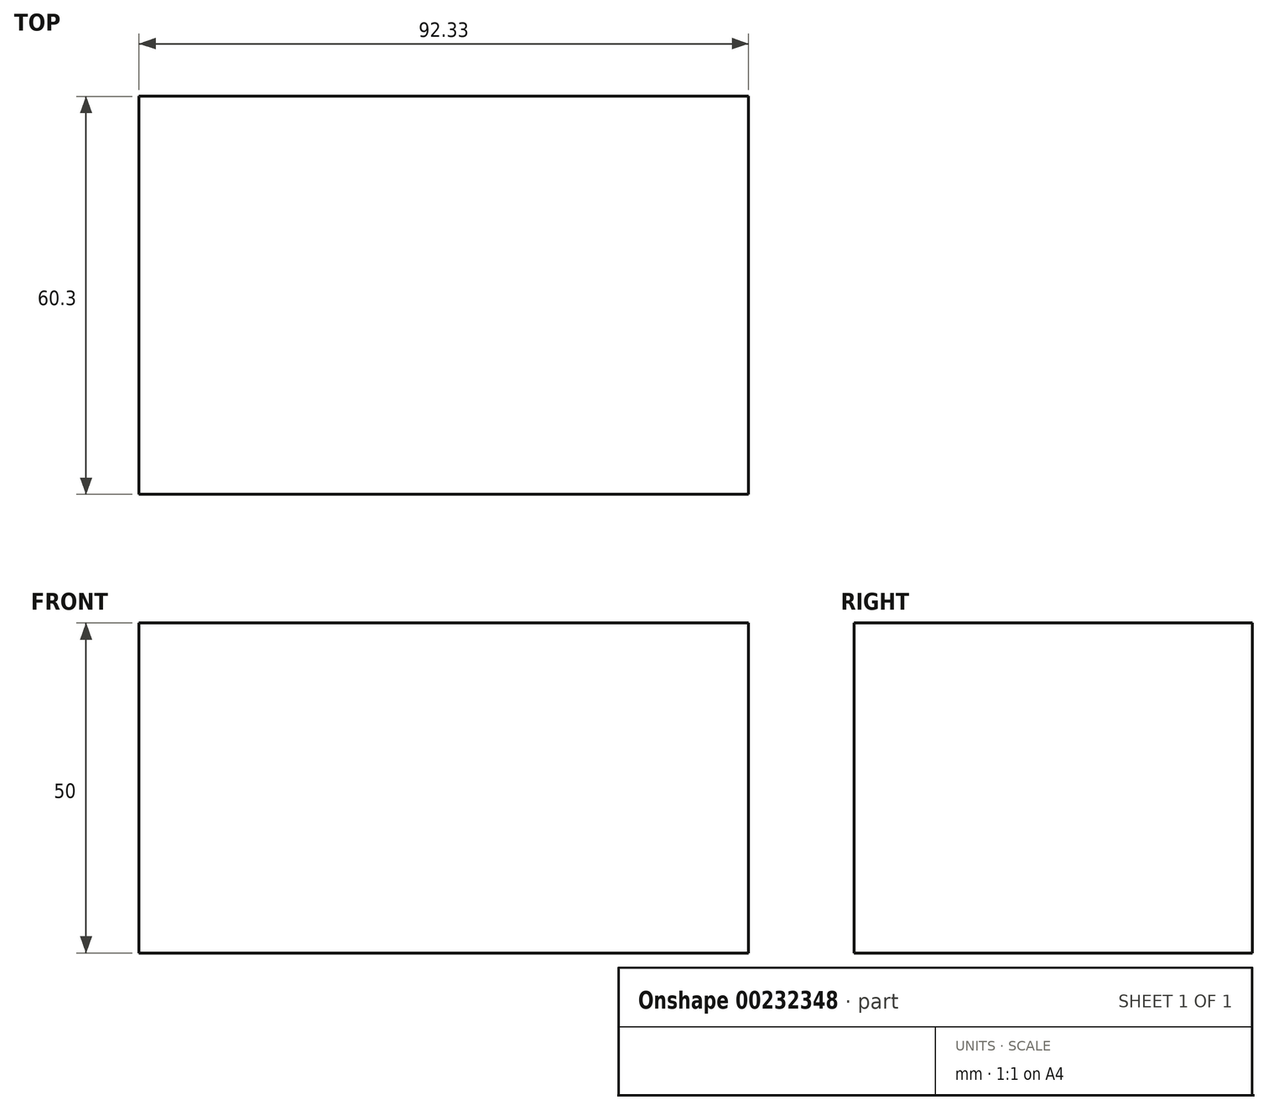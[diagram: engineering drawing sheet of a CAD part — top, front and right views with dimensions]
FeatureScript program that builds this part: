
annotation { "Feature Type Name" : "Feature", "Feature Type Description" : "" }
export const myFeature = defineFeature(function(context is Context, id is Id, definition is map)
    precondition{}
    {
        {
            var Q0;
            Q0=qCreatedBy(makeId("Top.planeOp"),FACE);
            var sketch = newSketch(context, id + "F0", { "sketchPlane" : qUnion([Q0])});
            skLineSegment(sketch, "E0.bottom", {"start": v(-53.56, 32.5) * mm, "end": v(38.77, 32.5) * mm});
            skLineSegment(sketch, "E0.top", {"start": v(-53.56, -27.81) * mm, "end": v(38.77, -27.81) * mm});
            skLineSegment(sketch, "E0.left", {"start": v(-53.56, 32.5) * mm, "end": v(-53.56, -27.81) * mm});
            skLineSegment(sketch, "E0.right", {"start": v(38.77, 32.5) * mm, "end": v(38.77, -27.81) * mm});
            skSolve(sketch);
        }
        {
            var Q0;
            Q0=makeQuery(id+"F0.imprint","IMPRINT",FACE,{"disambiguationData":[TD([[makeQuery(id+"F0.imprint","IMPRINT",EDGE,{"derivedFrom":sQuery(id+"F0.wireOp",EDGE,"E0.bottom")}),-1.0]])]});
            extrude(context, id + "F1", {"entities" : qUnion([Q0]), "depth" : 50 * mm});
        }
    });
